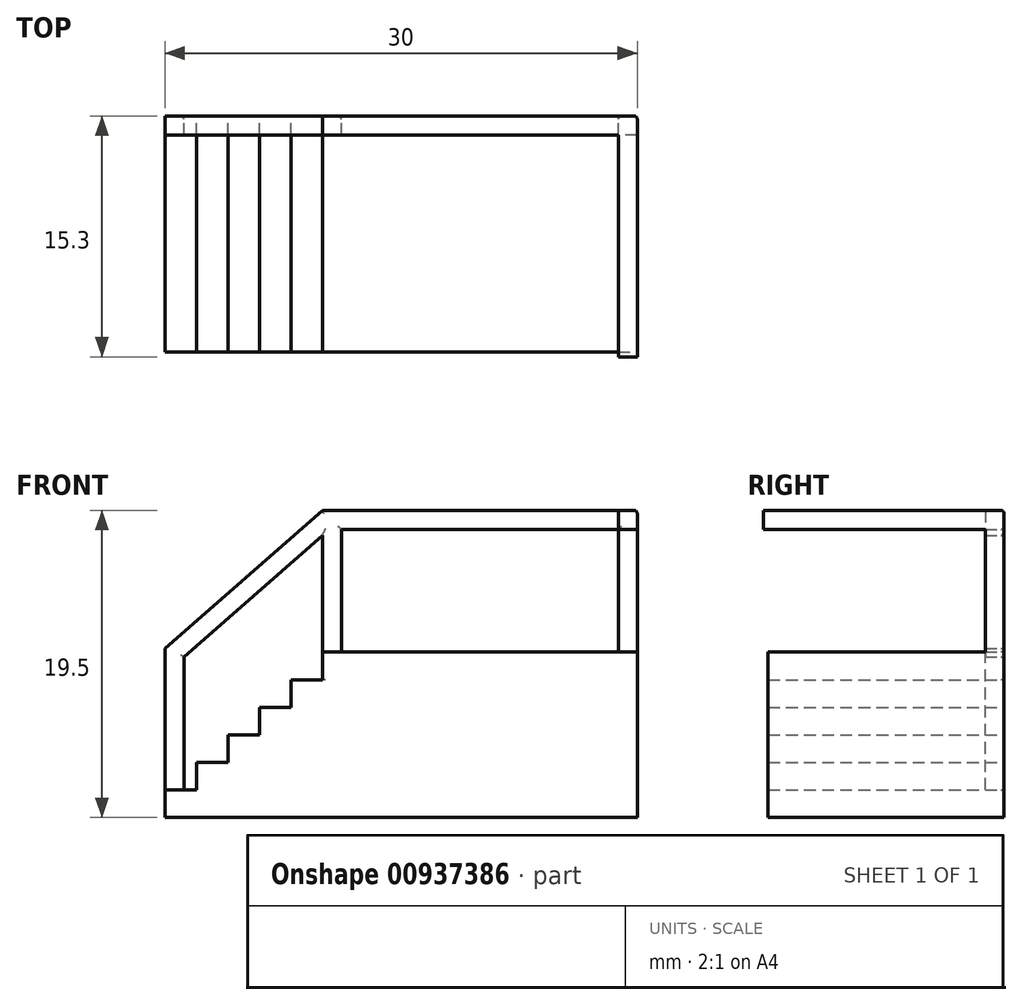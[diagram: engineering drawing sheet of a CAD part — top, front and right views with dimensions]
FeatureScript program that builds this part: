
annotation { "Feature Type Name" : "Feature", "Feature Type Description" : "" }
export const myFeature = defineFeature(function(context is Context, id is Id, definition is map)
    precondition{}
    {
        {
            var Q0;
            Q0=qCreatedBy(makeId("Front.planeOp"),FACE);
            var sketch = newSketch(context, id + "F0", { "sketchPlane" : qUnion([Q0])});
            skLineSegment(sketch, "E0", {"start": v(-71.5, 0) * mm, "end": v(-71.5, 1.75) * mm});
            skLineSegment(sketch, "E1", {"start": v(-71.5, 1.75) * mm, "end": v(-69.5, 1.75) * mm});
            skLineSegment(sketch, "E2", {"start": v(-69.5, 1.75) * mm, "end": v(-69.5, 3.5) * mm});
            skLineSegment(sketch, "E3", {"start": v(-69.5, 3.5) * mm, "end": v(-67.5, 3.5) * mm});
            skLineSegment(sketch, "E4", {"start": v(-67.5, 3.5) * mm, "end": v(-67.5, 5.25) * mm});
            skLineSegment(sketch, "E5", {"start": v(-67.5, 5.25) * mm, "end": v(-65.5, 5.25) * mm});
            skLineSegment(sketch, "E6", {"start": v(-65.5, 5.25) * mm, "end": v(-65.5, 7) * mm});
            skLineSegment(sketch, "E7", {"start": v(-65.5, 7) * mm, "end": v(-63.5, 7) * mm});
            skLineSegment(sketch, "E8", {"start": v(-63.5, 7) * mm, "end": v(-63.5, 8.75) * mm});
            skLineSegment(sketch, "E9", {"start": v(-63.5, 8.75) * mm, "end": v(-61.5, 8.75) * mm});
            skLineSegment(sketch, "E10", {"start": v(-61.5, 8.75) * mm, "end": v(-61.5, 10.5) * mm});
            skLineSegment(sketch, "E11", {"start": v(-61.5, 10.5) * mm, "end": v(-59.5, 10.5) * mm});
            skLineSegment(sketch, "E12", {"start": v(-59.5, 10.5) * mm, "end": v(-59.5, 12.25) * mm});
            skLineSegment(sketch, "E13", {"start": v(-59.5, 12.25) * mm, "end": v(-57.5, 12.25) * mm});
            skLineSegment(sketch, "E14", {"start": v(-57.5, 12.25) * mm, "end": v(-57.5, 14) * mm});
            skLineSegment(sketch, "E15", {"start": v(-57.5, 14) * mm, "end": v(-55.5, 14) * mm});
            skLineSegment(sketch, "E16", {"start": v(-55.5, 14) * mm, "end": v(-55.5, 15.75) * mm});
            skLineSegment(sketch, "E17", {"start": v(-55.5, 15.75) * mm, "end": v(-53.5, 15.75) * mm});
            skLineSegment(sketch, "E18", {"start": v(-53.5, 15.75) * mm, "end": v(-53.5, 17.5) * mm});
            skLineSegment(sketch, "E19", {"start": v(-39.5, 0) * mm, "end": v(-71.5, 0) * mm});
            skLineSegment(sketch, "E20", {"start": v(-53.5, 17.5) * mm, "end": v(-53.5, 26.5) * mm});
            skLineSegment(sketch, "E21", {"start": v(-71.5, 1.75) * mm, "end": v(-71.5, 10.75) * mm});
            skLineSegment(sketch, "E22", {"start": v(-71.5, 10.75) * mm, "end": v(-53.5, 26.5) * mm});
            skLineSegment(sketch, "E23", {"start": v(-53.5, 26.5) * mm, "end": v(-52.3, 26.5) * mm});
            skLineSegment(sketch, "E24", {"start": v(-52.3, 26.5) * mm, "end": v(-52.3, 17.5) * mm});
            skLineSegment(sketch, "E25", {"start": v(-52.3, 26.5) * mm, "end": v(-52.3, 26) * mm});
            skLineSegment(sketch, "E26", {"start": v(-71.5, 10.75) * mm, "end": v(-70.3, 10.75) * mm});
            skLineSegment(sketch, "E27", {"start": v(-70.3, 10.75) * mm, "end": v(-70.3, 1.75) * mm});
            skLineSegment(sketch, "E28", {"start": v(-63.5, 8.75) * mm, "end": v(-63.5, 17.09) * mm});
            skLineSegment(sketch, "E29", {"start": v(-63.5, 8.75) * mm, "end": v(-62.3, 8.75) * mm});
            skLineSegment(sketch, "E30", {"start": v(-62.3, 8.75) * mm, "end": v(-62.3, 18.14) * mm});
            skLineSegment(sketch, "E31", {"start": v(-63.5, 17.09) * mm, "end": v(-63.5, 17.75) * mm});
            skLineSegment(sketch, "E32", {"start": v(-61.37, 19.61) * mm, "end": v(-60.58, 18.7) * mm});
            skLineSegment(sketch, "E33", {"start": v(-60.58, 18.7) * mm, "end": v(-53.5, 24.9) * mm});
            skLineSegment(sketch, "E34", {"start": v(-60.58, 18.7) * mm, "end": v(-70.3, 10.2) * mm});
            skLineSegment(sketch, "E35", {"start": v(-63.5, 7) * mm, "end": v(-37, 7) * mm});
            skLineSegment(sketch, "E36", {"start": v(-53.5, 26.5) * mm, "end": v(-33.5, 26.5) * mm});
            skLineSegment(sketch, "E37", {"start": v(-33.5, 26.5) * mm, "end": v(-33.5, 0) * mm});
            skLineSegment(sketch, "E38", {"start": v(-37, 7) * mm, "end": v(-33.5, 7) * mm});
            skLineSegment(sketch, "E39", {"start": v(-53.5, 17.5) * mm, "end": v(-33.5, 17.5) * mm});
            skLineSegment(sketch, "E40", {"start": v(-33.5, 26.5) * mm, "end": v(-34.7, 26.5) * mm});
            skLineSegment(sketch, "E41", {"start": v(-34.7, 26.5) * mm, "end": v(-34.7, 17.5) * mm});
            skLineSegment(sketch, "E42", {"start": v(-34.7, 26.5) * mm, "end": v(-34.7, 25.3) * mm});
            skLineSegment(sketch, "E43", {"start": v(-34.7, 25.3) * mm, "end": v(-52.3, 25.3) * mm});
            skSolve(sketch);
        }
        {
            var Q0;
            {var subQ0=sQuery(id+"F0.wireOp",EDGE,"E8");Q0=makeQuery(id+"F0.imprint","IMPRINT",FACE,{"disambiguationData":[TD([[makeQuery(id+"F0.imprint","IMPRINT",EDGE,{"derivedFrom":subQ0}),-1.0]])]});}
            var Q1;
            {var subQ0=sQuery(id+"F0.wireOp",EDGE,"E8");Q1=makeQuery(id+"F0.imprint","IMPRINT",FACE,{"disambiguationData":[TD([[makeQuery(id+"F0.imprint","IMPRINT",EDGE,{"derivedFrom":subQ0}),-1.0]])]});}
            extrude(context, id + "F1", {"entities" : qUnion([Q0, Q1]), "depth" : 15 * mm, "offsetDistance" : 25 * mm});
        }
        {
            var Q0;
            {var subQ1=sQuery(id+"F0.wireOp",EDGE,"E31");Q0=makeQuery(id+"F0.imprint","IMPRINT",FACE,{"disambiguationData":[TD([[makeQuery(id+"F0.imprint","IMPRINT",EDGE,{"derivedFrom":subQ1}),-1.0]])]});}
            var Q1;
            {var subQ1=sQuery(id+"F0.wireOp",EDGE,"E9");var subQ3=sQuery(id+"F0.wireOp",EDGE,"E30");var subQ4=makeQuery(id+"F0.imprint","INTERSECT",VERTEX,{"derivedFrom":[subQ1,subQ3]});Q1=makeQuery(id+"F0.imprint","IMPRINT",FACE,{"disambiguationData":[TD([[makeQuery(id+"F0.imprint","IMPRINT",EDGE,{"disambiguationData":[TD([[subQ4,-1.0]])],"derivedFrom":subQ3}),1.0]])]});}
            var Q2;
            {var subQ0=sQuery(id+"F0.wireOp",EDGE,"E23");Q2=makeQuery(id+"F0.imprint","IMPRINT",FACE,{"disambiguationData":[TD([[makeQuery(id+"F0.imprint","IMPRINT",EDGE,{"derivedFrom":subQ0}),-1.0]])]});}
            var Q3;
            {var subQ0=sQuery(id+"F0.wireOp",EDGE,"fYkq94Di-rKUo-Wbgf-4JCa-c6ZceNlMfAkK");Q3=makeQuery(id+"F0.imprint","IMPRINT",FACE,{"disambiguationData":[TD([[makeQuery(id+"F0.imprint","IMPRINT",EDGE,{"derivedFrom":subQ0}),1.0]])]});}
            var Q4;
            {var subQ3=sQuery(id+"F0.wireOp",EDGE,"A2OyEonq-wSMN-l8rg-RSiw-ENtH85iaNFeu");Q4=makeQuery(id+"F0.imprint","IMPRINT",FACE,{"disambiguationData":[TD([[makeQuery(id+"F0.imprint","IMPRINT",EDGE,{"derivedFrom":subQ3}),1.0]])]});}
            var Q5;
            {var subQ4=sQuery(id+"F0.wireOp",EDGE,"E32");Q5=makeQuery(id+"F0.imprint","IMPRINT",FACE,{"disambiguationData":[TD([[makeQuery(id+"F0.imprint","IMPRINT",EDGE,{"derivedFrom":subQ4}),1.0]])]});}
            var Q6;
            {var subQ0=sQuery(id+"F0.wireOp",EDGE,"E43");Q6=makeQuery(id+"F0.imprint","IMPRINT",FACE,{"disambiguationData":[TD([[makeQuery(id+"F0.imprint","IMPRINT",EDGE,{"derivedFrom":subQ0}),-1.0]])]});}
            var Q7;
            {var subQ5=sQuery(id+"F0.wireOp",EDGE,"NjBgZ1He-fScK-0ryk-p2vt-0fSinNFSWKJH");Q7=makeQuery(id+"F0.imprint","IMPRINT",FACE,{"disambiguationData":[TD([[makeQuery(id+"F0.imprint","IMPRINT",EDGE,{"derivedFrom":subQ5}),1.0]])]});}
            var Q8;
            {var subQ1=sQuery(id+"F0.wireOp",EDGE,"E37");var subQ6=sQuery(id+"F0.wireOp",EDGE,"E36");var subQ7=makeQuery(id+"F0.imprint","INTERSECT",VERTEX,{"derivedFrom":[subQ6,subQ1]});Q8=makeQuery(id+"F0.imprint","IMPRINT",FACE,{"disambiguationData":[TD([[makeQuery(id+"F0.imprint","IMPRINT",EDGE,{"disambiguationData":[TD([[subQ7,1.0]])],"derivedFrom":subQ6}),-1.0]])]});}
            var Q9;
            {var subQ6=sQuery(id+"F0.wireOp",EDGE,"E23");Q9=makeQuery(id+"F0.imprint","IMPRINT",FACE,{"disambiguationData":[TD([[makeQuery(id+"F0.imprint","IMPRINT",EDGE,{"derivedFrom":subQ6}),-1.0]])]});}
            extrude(context, id + "F2", {"entities" : qUnion([Q0, Q1, Q2, Q3, Q4, Q5, Q6, Q7, Q8, Q9]), "operationType" : NewBodyOperationType.ADD, "depth" : 1.2 * mm, "offsetDistance" : 25 * mm});
        }
        {
            var Q0;
            Q0=makeQuery(id+"F2.opExtrude","CAP_FACE",FACE,{"disambiguationData":[OSD([sQuery(id+"F0.wireOp",EDGE,"E9"),sQuery(id+"F0.wireOp",EDGE,"E20"),sQuery(id+"F0.wireOp",EDGE,"E22"),sQuery(id+"F0.wireOp",EDGE,"E23"),sQuery(id+"F0.wireOp",EDGE,"E24"),sQuery(id+"F0.wireOp",EDGE,"E28"),sQuery(id+"F0.wireOp",EDGE,"E30"),sQuery(id+"F0.wireOp",EDGE,"E31"),sQuery(id+"F0.wireOp",EDGE,"E33"),sQuery(id+"F0.wireOp",EDGE,"E34"),sQuery(id+"F0.wireOp",EDGE,"E36"),sQuery(id+"F0.wireOp",EDGE,"E37"),sQuery(id+"F0.wireOp",EDGE,"E39"),sQuery(id+"F0.wireOp",EDGE,"E41"),sQuery(id+"F0.wireOp",EDGE,"E43")])],"isStart":false});
            var sketch = newSketch(context, id + "F3", { "sketchPlane" : qUnion([Q0])});
            skLineSegment(sketch, "E44.bottom", {"start": v(-33.5, 26.5) * mm, "end": v(-34.7, 26.5) * mm});
            skLineSegment(sketch, "E44.top", {"start": v(-33.5, 25.3) * mm, "end": v(-34.7, 25.3) * mm});
            skLineSegment(sketch, "E44.left", {"start": v(-33.5, 26.5) * mm, "end": v(-33.5, 25.3) * mm});
            skLineSegment(sketch, "E44.right", {"start": v(-34.7, 26.5) * mm, "end": v(-34.7, 25.3) * mm});
            skSolve(sketch);
        }
        {
            var Q0;
            Q0=makeQuery(id+"F3.imprint","IMPRINT",FACE,{"disambiguationData":[TD([[makeQuery(id+"F3.imprint","IMPRINT",EDGE,{"derivedFrom":sQuery(id+"F3.wireOp",EDGE,"E44.bottom")}),-1.0]])]});
            extrude(context, id + "F4", {"entities" : qUnion([Q0]), "operationType" : NewBodyOperationType.ADD, "depth" : 14.1 * mm, "offsetDistance" : 25 * mm});
        }
        {
            var Q0;
            Q0=makeQuery(id+"F2.opExtrude","CAP_EDGE",EDGE,{"disambiguationData":[OSD([sQuery(id+"F0.wireOp",EDGE,"E43")])],"isStart":true});
            var Q1;
            Q1=makeQuery(id+"F2.opExtrude","CAP_EDGE",EDGE,{"disambiguationData":[OSD([sQuery(id+"F0.wireOp",EDGE,"E41")])],"isStart":true});
            var Q2;
            Q2=makeQuery(id+"F2.opExtrude","CAP_EDGE",EDGE,{"disambiguationData":[OSD([sQuery(id+"F0.wireOp",EDGE,"E24")])],"isStart":true});
            var Q3;
            Q3=makeQuery(id+"F2.opExtrude","CAP_EDGE",EDGE,{"disambiguationData":[OSD([sQuery(id+"F0.wireOp",EDGE,"E33"),sQuery(id+"F0.wireOp",EDGE,"E34")])],"isStart":true});
            var Q4;
            Q4=makeQuery(id+"F2.boolean.opBoolean","MERGE",EDGE,{"derivedFrom":[makeQuery(id+"F1.opExtrude","CAP_EDGE",EDGE,{"disambiguationData":[OSD([sQuery(id+"F0.wireOp",EDGE,"E18")])],"isStart":true}),makeQuery(id+"F2.opExtrude","CAP_EDGE",EDGE,{"disambiguationData":[OSD([sQuery(id+"F0.wireOp",EDGE,"E20")])],"isStart":true})]});
            var Q5;
            Q5=makeQuery(id+"F2.opExtrude","CAP_EDGE",EDGE,{"disambiguationData":[OSD([sQuery(id+"F0.wireOp",EDGE,"E30")])],"isStart":true});
            var Q6;
            Q6=makeQuery(id+"F2.opExtrude","CAP_EDGE",EDGE,{"disambiguationData":[OSD([sQuery(id+"F0.wireOp",EDGE,"E22")])],"isStart":true});
            var Q7;
            Q7=makeQuery(id+"F2.opExtrude","CAP_EDGE",EDGE,{"disambiguationData":[OSD([sQuery(id+"F0.wireOp",EDGE,"E23"),sQuery(id+"F0.wireOp",EDGE,"E36")])],"isStart":true});
            var Q8;
            {var subQ0=sQuery(id+"F0.wireOp",EDGE,"E37");Q8=makeQuery(id+"F2.boolean.opBoolean","MERGE",EDGE,{"derivedFrom":[makeQuery(id+"F1.opExtrude","CAP_EDGE",EDGE,{"disambiguationData":[OSD([subQ0])],"isStart":true}),makeQuery(id+"F2.opExtrude","CAP_EDGE",EDGE,{"disambiguationData":[OSD([subQ0])],"isStart":true})]});}
            var Q9;
            Q9=makeQuery(id+"F4.boolean.opBoolean","MERGE",EDGE,{"derivedFrom":[makeQuery(id+"F2.opExtrude","SWEPT_EDGE",EDGE,{"disambiguationData":[OSD([sQuery(id+"F0.wireOp",EDGE,"E36"),sQuery(id+"F0.wireOp",EDGE,"E37")])]}),makeQuery(id+"F4.opExtrude","SWEPT_EDGE",EDGE,{"disambiguationData":[OSD([sQuery(id+"F3.wireOp",EDGE,"E44.bottom"),sQuery(id+"F3.wireOp",EDGE,"E44.left")])]})]});
            fillet(context, id + "F5", {"entities" : qUnion([Q0, Q1, Q2, Q3, Q4, Q5, Q6, Q7, Q8, Q9]), "radius" : .2 * mm, "tangentPropagation" : true, "allowEdgeOverflow" : false});
        }
    });
